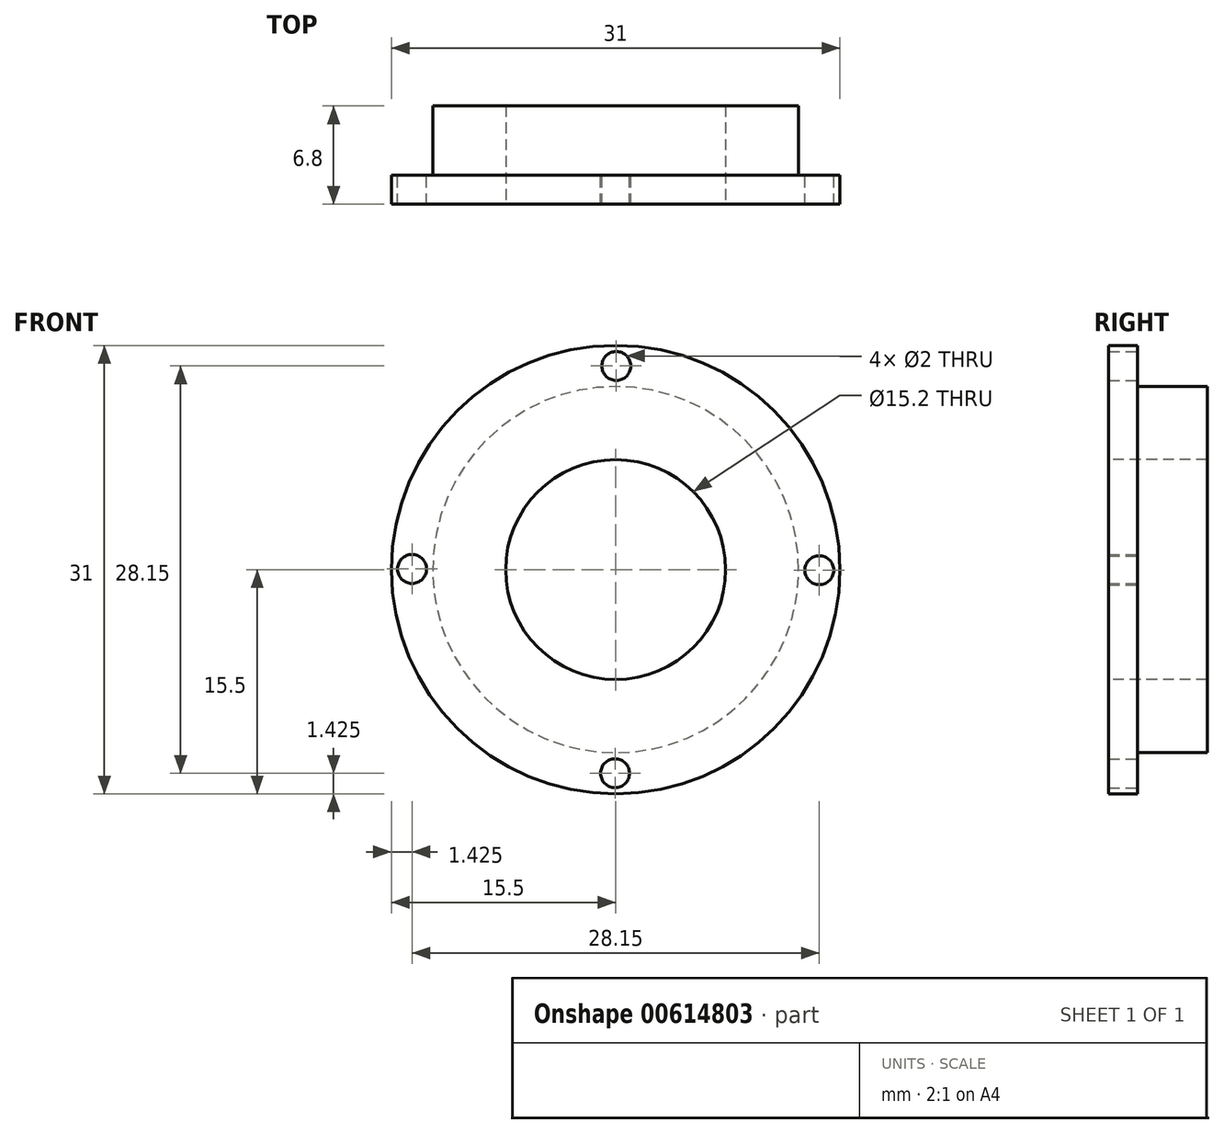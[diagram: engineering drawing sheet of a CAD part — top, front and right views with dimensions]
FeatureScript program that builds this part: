
annotation { "Feature Type Name" : "Feature", "Feature Type Description" : "" }
export const myFeature = defineFeature(function(context is Context, id is Id, definition is map)
    precondition{}
    {
        {
            var Q0;
            Q0=qCreatedBy(makeId("Front.planeOp"),FACE);
            var sketch = newSketch(context, id + "F0", { "sketchPlane" : qUnion([Q0])});
            skCircle(sketch, "E0", {"center": v(0, 0) * mm, "radius": 12.65 * mm});
            skSolve(sketch);
        }
        {
            var Q0;
            Q0 = qSketchRegion(id + "F0", true);
            var Q1;
            Q1 = qSketchRegion(id + "F2", true);
            extrude(context, id + "F1", {"entities" : qUnion([Q0, Q1]), "depth" : 4.8 * mm, "offsetDistance" : 25 * mm});
        }
        {
            var Q0;
            Q0=makeQuery(id+"F1.opExtrude","CAP_FACE",FACE,{"disambiguationData":[OSD([sQuery(id+"F0.wireOp",EDGE,"E0")])],"isStart":false});
            var sketch = newSketch(context, id + "F2", { "sketchPlane" : qUnion([Q0])});
            skCircle(sketch, "E1.0", {"center": v(0, 0) * mm, "radius": 12.65 * mm});
            skCircle(sketch, "E2", {"center": v(0, 0) * mm, "radius": 15.5 * mm});
            skSolve(sketch);
        }
        {
            var Q0;
            Q0 = qSketchRegion(id + "F2", true);
            var Q1;
            Q1=makeQuery(id+"F2.imprint","IMPRINT",FACE,{"disambiguationData":[TD([[makeQuery(id+"F2.imprint","IMPRINT",EDGE,{"derivedFrom":sQuery(id+"F2.wireOp",EDGE,"E1.0")}),1.0]])]});
            extrude(context, id + "F3", {"entities" : qUnion([Q0, Q1]), "operationType" : NewBodyOperationType.ADD, "depth" : 2 * mm, "offsetDistance" : 25 * mm});
        }
        {
            var Q0;
            Q0=makeQuery(id+"F3.opExtrude","CAP_FACE",FACE,{"disambiguationData":[OSD([sQuery(id+"F2.wireOp",EDGE,"E2")])],"isStart":true});
            var sketch = newSketch(context, id + "F4", { "sketchPlane" : qUnion([Q0])});
            skCircle(sketch, "E3.0", {"center": v(0, 0) * mm, "radius": 15.5 * mm});
            skCircle(sketch, "E4.0", {"center": v(0, 0) * mm, "radius": 12.65 * mm});
            skCircle(sketch, "E5", {"center": v(-0.04, 14.07) * mm, "radius": 1 * mm});
            skCircle(sketch, "E6.1.0", {"center": v(-14.07, -0.04) * mm, "radius": 1 * mm});
            skCircle(sketch, "E6.2.0", {"center": v(0.04, -14.07) * mm, "radius": 1 * mm});
            skCircle(sketch, "E6.3.0", {"center": v(14.07, 0.04) * mm, "radius": 1 * mm});
            skSolve(sketch);
        }
        {
            var Q0;
            Q0=makeQuery(id+"F4.imprint","IMPRINT",FACE,{"disambiguationData":[TD([[makeQuery(id+"F4.imprint","IMPRINT",EDGE,{"derivedFrom":sQuery(id+"F4.wireOp",EDGE,"E5")}),1.0]])]});
            var Q1;
            Q1=makeQuery(id+"F4.imprint","IMPRINT",FACE,{"disambiguationData":[TD([[makeQuery(id+"F4.imprint","IMPRINT",EDGE,{"derivedFrom":sQuery(id+"F4.wireOp",EDGE,"E6.1.0")}),1.0]])]});
            var Q2;
            Q2=makeQuery(id+"F4.imprint","IMPRINT",FACE,{"disambiguationData":[TD([[makeQuery(id+"F4.imprint","IMPRINT",EDGE,{"derivedFrom":sQuery(id+"F4.wireOp",EDGE,"E6.2.0")}),1.0]])]});
            var Q3;
            Q3=makeQuery(id+"F4.imprint","IMPRINT",FACE,{"disambiguationData":[TD([[makeQuery(id+"F4.imprint","IMPRINT",EDGE,{"derivedFrom":sQuery(id+"F4.wireOp",EDGE,"E6.3.0")}),1.0]])]});
            extrude(context, id + "F5", {"entities" : qUnion([Q0, Q1, Q2, Q3]), "operationType" : NewBodyOperationType.REMOVE, "oppositeDirection" : true, "depth" : 2 * mm, "offsetDistance" : 25 * mm});
        }
        {
            var Q0;
            Q0=makeQuery(id+"F3.opExtrude","CAP_FACE",FACE,{"disambiguationData":[OSD([sQuery(id+"F2.wireOp",EDGE,"E2")])],"isStart":false});
            var sketch = newSketch(context, id + "F6", { "sketchPlane" : qUnion([Q0])});
            skCircle(sketch, "E7.0", {"center": v(0, 0) * mm, "radius": 15.5 * mm});
            skCircle(sketch, "E8", {"center": v(0, 0) * mm, "radius": 7.6 * mm});
            skSolve(sketch);
        }
        {
            var Q0;
            Q0=makeQuery(id+"F6.imprint","IMPRINT",FACE,{"disambiguationData":[TD([[makeQuery(id+"F6.imprint","IMPRINT",EDGE,{"derivedFrom":sQuery(id+"F6.wireOp",EDGE,"E8")}),1.0]])]});
            extrude(context, id + "F7", {"entities" : qUnion([Q0]), "operationType" : NewBodyOperationType.REMOVE, "oppositeDirection" : true, "depth" : 7 * mm, "offsetDistance" : 25 * mm});
        }
    });
